# Revit family: Flood-Barrier_Removeable_WalzKrenzer_Inflatable
name_source: partatom
category: Generic Models
units: mm (PartAtom-declared; Revit-internal decimal feet)

## family parameters
Can host rebar = No
Classification Number = 23.30.10.21.37.17
Cut with Voids When Loaded = No
Host = Face
Maintain Annotation Orientation = No
Part Type = Normal
Room Calculation Point = No
Round Connector Dimension = Use Diameter
Shared = No

## types (2) — shared parameters
Assembly Code = E1090900
Default Elevation = 0' - 0"
Description = Walz and Krenzer Removeable Flood Barrier - Inflatable Gasket FP-I as Specified
Keynote = 08392
Manufacturer = Walz & Krenzer, Inc.
Manufacturer Fax = 203-267-5716
Manufacturer Website = http://www.floodbarriers.com
Model = FP-I
Product Data = http://www.arcat.com
Revision = R1_2015-06
Sales Information = http://www.floodbarriers.com
Specification = http://www.arcat.com
Test Data = http://www.floodbarriers.com
URL = http://www.floodbarriers.com
zero-valued in all types: Expected Lifespan (Years), Maintenance Schedule (Months), Warranty Duration (Years)

## type names (no varying parameters)
- Double Gasket
- Single Gasket

## geometry (parser evidence)
native form markers: Sweep x10
no freeform markers — native parametric forms only
